# Revit family: Table-Casual-Teknion-ATCCC-Circular_Cafe-R2018
name_source: partatom
category: Furniture
revit_build: Autodesk Revit 2018 (Build: 20190510_1515(x64)
units: mm (PartAtom-declared; Revit-internal decimal feet)

## family parameters
Always vertical = Yes
Cut with Voids When Loaded = No
OmniClass Number = 23.40.20.00
OmniClass Title = General Furniture and Specialties
Room Calculation Point = No
Shared = Yes
Work Plane-Based = No

## types (2) — shared parameters
Assembly Code = E2020200
Manufacturer = Teknion
Manufacturer Fax = 416.661.4586
Part Number = ATCCC
Product Documentation Link = http://www.teknion.com
Product Line = Tables & Collaborative Spaces
Product Page URL = http://www.teknion.com
Series = Tables & Collaborative Spaces
Sustainability Data = http://www.teknion.com
URL = www.teknion.com
Unit Weight URL = http://www.teknion.com
Warranty = http://www.teknion.com

## per-type parameters (varying)
| type | Description | Diameter | Model | Radius |
| 24" Diameter | Circular Cafe Table, 24" Diameter | 24 " | ATCCC24 | 12 " |
| 30" Diameter | Circular Cafe Table, 30" Diameter | 30 " | ATCCC30 | 15 " |

## geometry (parser evidence)
native form markers: Blend x2, Sweep x2
no freeform markers — native parametric forms only
